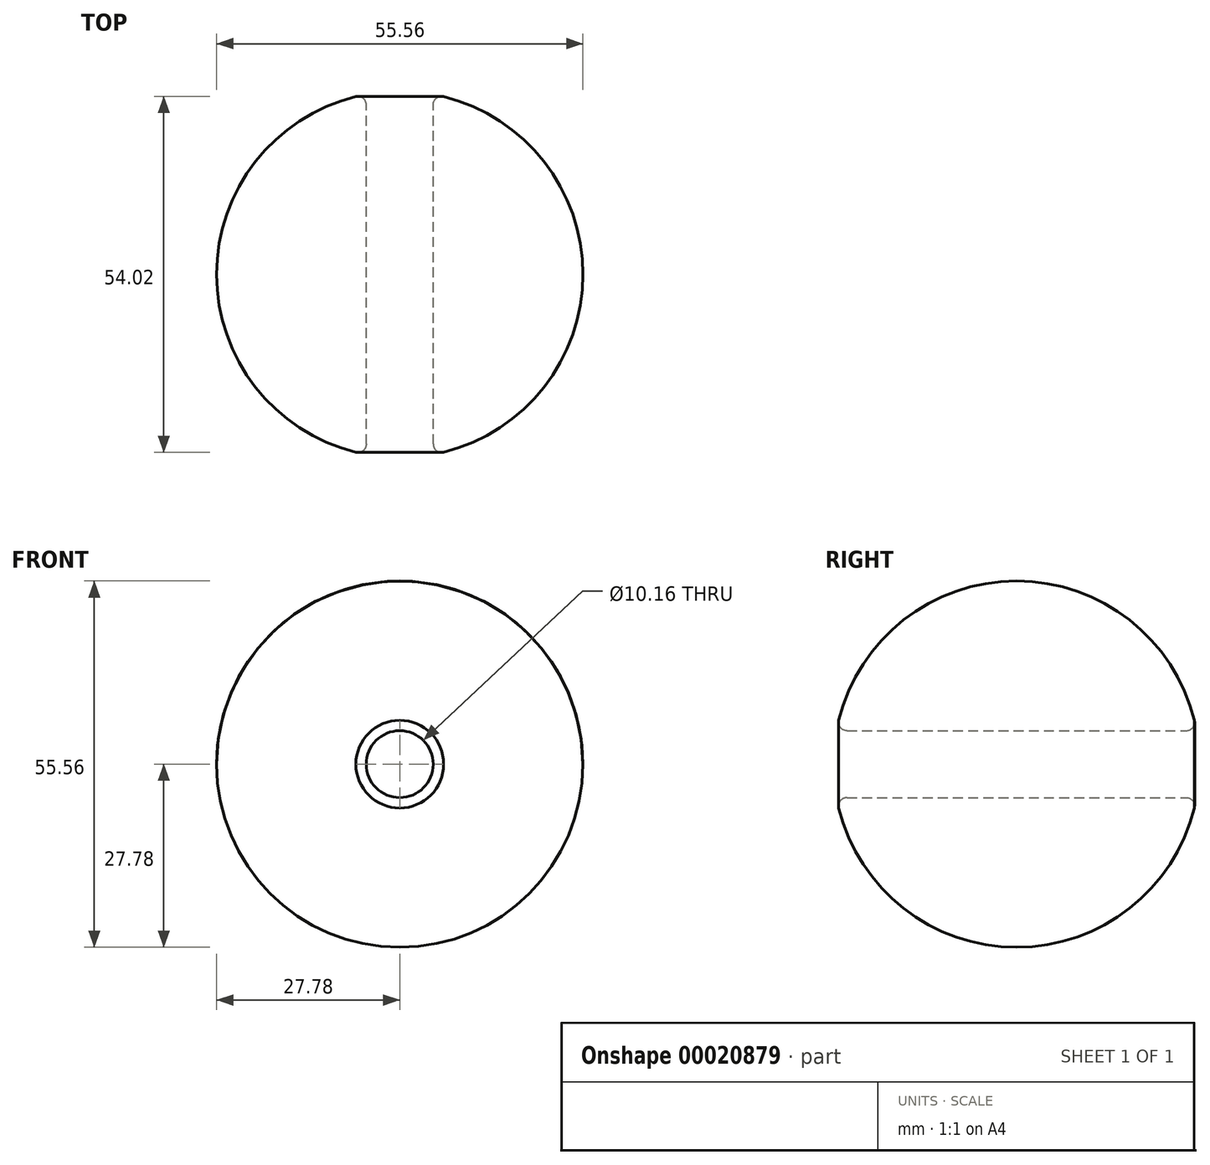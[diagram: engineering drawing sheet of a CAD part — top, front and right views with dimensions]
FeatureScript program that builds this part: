
annotation { "Feature Type Name" : "Feature", "Feature Type Description" : "" }
export const myFeature = defineFeature(function(context is Context, id is Id, definition is map)
    precondition{}
    {
        {
            var Q0;
            Q0=qCreatedBy(makeId("Front.planeOp"),FACE);
            var sketch = newSketch(context, id + "F0", { "sketchPlane" : qUnion([Q0])});
            skArc(sketch, "E0", {"start": v(27.78, 0) * mm, "mid": v(0, 27.78) * mm, "end": v(-27.78, 0) * mm});
            skLineSegment(sketch, "E1", {"start": v(-27.78, 0) * mm, "end": v(27.78, 0) * mm});
            skArc(sketch, "E2", {"start": v(5.08, 0) * mm, "mid": v(0, 5.08) * mm, "end": v(-5.08, 0) * mm});
            skSolve(sketch);
        }
        {
            var Q0;
            Q0 = qSketchRegion(id + "F0", true);
            var Q1;
            Q1=sQuery(id+"F0.wireOp",EDGE,"E1");
            revolve(context, id + "F1", {"entities" : qUnion([Q0]), "axis" : qUnion([Q1]), "revolveType" : RevolveType.FULL});
        }
        {
            var Q0;
            Q0=qCreatedBy(makeId("Front.planeOp"),FACE);
            var sketch = newSketch(context, id + "F2", { "sketchPlane" : qUnion([Q0])});
            skCircle(sketch, "E3", {"center": v(0, 0) * mm, "radius": 5.08 * mm});
            skSolve(sketch);
        }
        {
            var Q0;
            Q0 = qSketchRegion(id + "F2", true);
            extrude(context, id + "F3", {"entities" : qUnion([Q0]), "operationType" : NewBodyOperationType.REMOVE, "endBound" : BoundingType.THROUGH_ALL, "depth" : 25.4 * mm});
        }
        {
            var Q0;
            Q0 = qSketchRegion(id + "F2", true);
            extrude(context, id + "F4", {"entities" : qUnion([Q0]), "operationType" : NewBodyOperationType.REMOVE, "endBound" : BoundingType.THROUGH_ALL, "oppositeDirection" : true, "depth" : 25.4 * mm});
        }
        {
            var Q0;
            Q0=makeQuery(id+"F4.boolean.opBoolean","INTERSECT",EDGE,{"derivedFrom":[makeQuery(id+"F1.opRevolve","SWEPT_FACE",FACE,{"disambiguationData":[OSD([sQuery(id+"F0.wireOp",EDGE,"E0")])]}),makeQuery(id+"F4.opExtrude","SWEPT_FACE",FACE,{"disambiguationData":[OSD([sQuery(id+"F2.wireOp",EDGE,"E3")])]})]});
            fillet(context, id + "F5", {"entities" : qUnion([Q0]), "radius" : 1.27 * mm, "tangentPropagation" : true, "allowEdgeOverflow" : false});
        }
        {
            var Q0;
            {var subQ0=sQuery(id+"F2.wireOp",EDGE,"E3");Q0=makeQuery(id+"F4.boolean.opBoolean","MERGE",FACE,{"derivedFrom":[makeQuery(id+"F3.boolean.opBoolean","COPY",FACE,{"derivedFrom":makeQuery(id+"F3.opExtrude","SWEPT_FACE",FACE,{"disambiguationData":[OSD([subQ0])]})}),makeQuery(id+"F4.opExtrude","SWEPT_FACE",FACE,{"disambiguationData":[OSD([subQ0])]})]});}
            fillet(context, id + "F6", {"entities" : qUnion([Q0]), "radius" : 1.27 * mm, "tangentPropagation" : true, "allowEdgeOverflow" : false});
        }
    });
